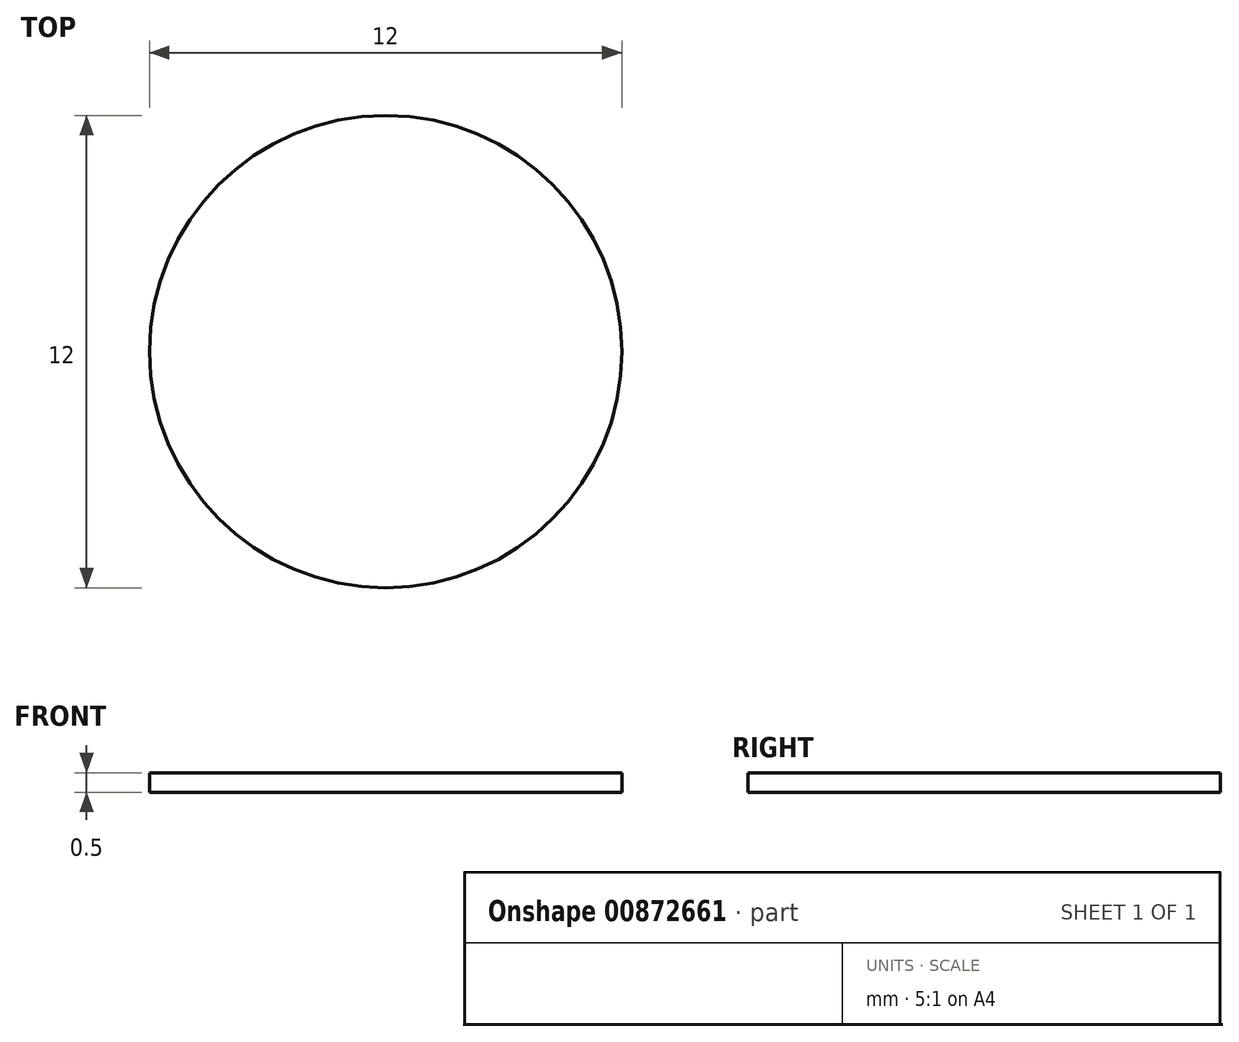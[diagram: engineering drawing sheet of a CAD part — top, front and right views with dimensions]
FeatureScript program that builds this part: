
annotation { "Feature Type Name" : "Feature", "Feature Type Description" : "" }
export const myFeature = defineFeature(function(context is Context, id is Id, definition is map)
    precondition{}
    {
        {
            var Q0;
            Q0=qCreatedBy(makeId("Top.planeOp"),FACE);
            var sketch = newSketch(context, id + "F0", { "sketchPlane" : qUnion([Q0])});
            skCircle(sketch, "E0", {"center": v(0, 0) * mm, "radius": 6 * mm});
            skSolve(sketch);
        }
        {
            var Q0;
            Q0 = qSketchRegion(id + "F0", true);
            extrude(context, id + "F1", {"entities" : qUnion([Q0]), "depth" : .5 * mm, "offsetDistance" : 25 * mm});
        }
    });
